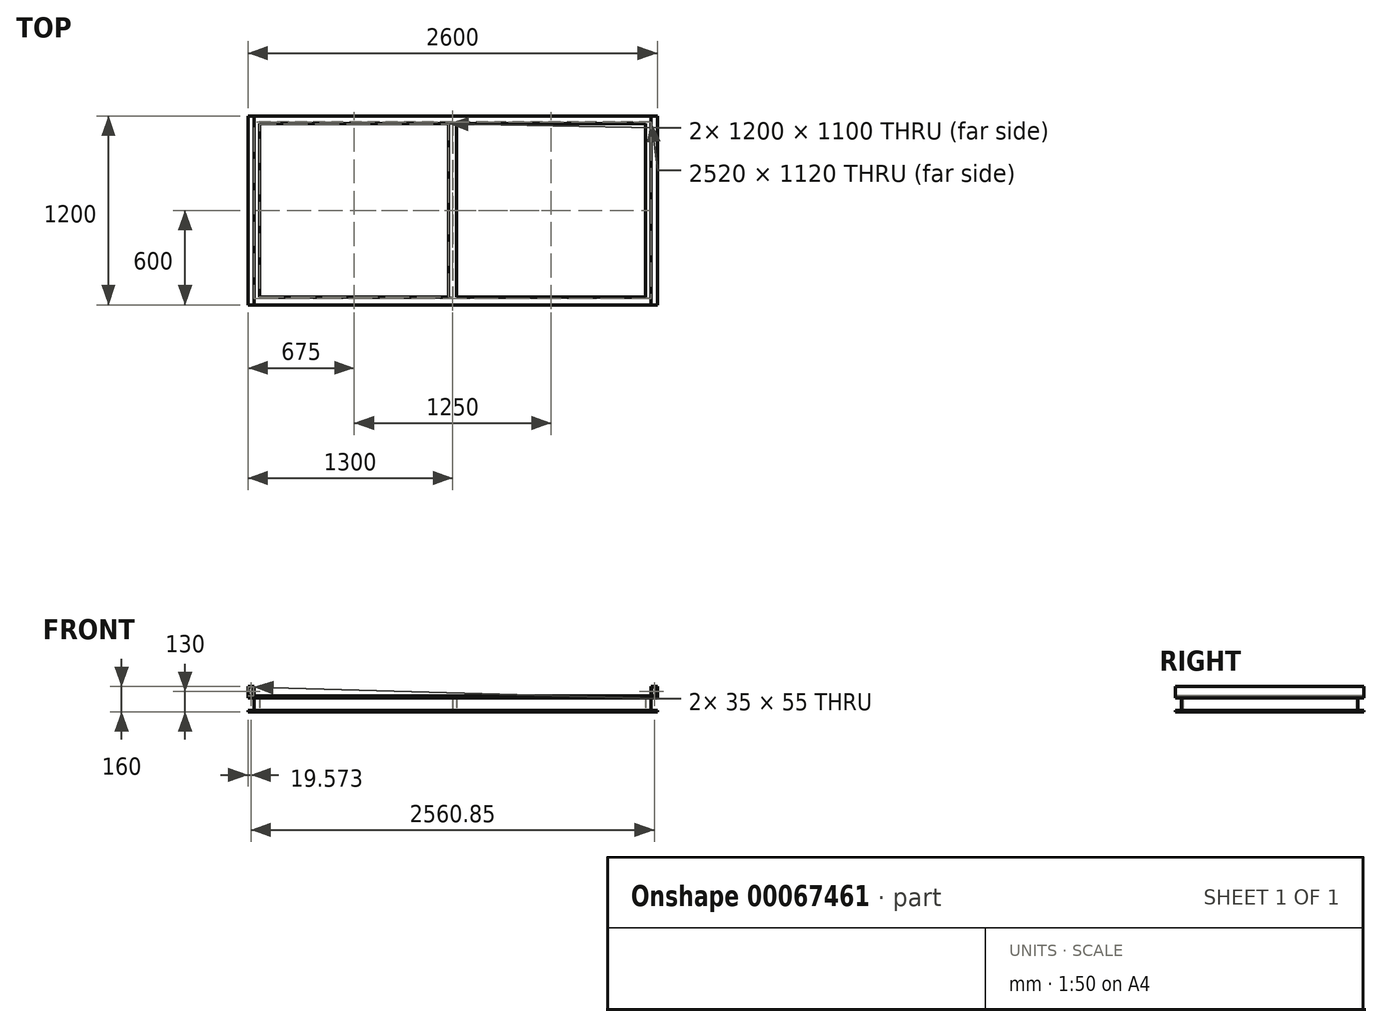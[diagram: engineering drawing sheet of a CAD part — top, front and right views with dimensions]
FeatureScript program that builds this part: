
annotation { "Feature Type Name" : "Feature", "Feature Type Description" : "" }
export const myFeature = defineFeature(function(context is Context, id is Id, definition is map)
    precondition{}
    {
        {
            var Q0;
            Q0=qCreatedBy(makeId("Top.planeOp"),FACE);
            var sketch = newSketch(context, id + "F0", { "sketchPlane" : qUnion([Q0])});
            skLineSegment(sketch, "E0.rect.bottom", {"start": v(1300, 600) * mm, "end": v(-1300, 600) * mm});
            skLineSegment(sketch, "E0.rect.top", {"start": v(1300, -600) * mm, "end": v(-1300, -600) * mm});
            skLineSegment(sketch, "E0.rect.left", {"start": v(1300, 600) * mm, "end": v(1300, -600) * mm});
            skLineSegment(sketch, "E0.rect.right", {"start": v(-1300, 600) * mm, "end": v(-1300, -600) * mm});
            skPoint(sketch, "E0.rect.middle", {"position": v(0, 0) * mm});
            skLineSegment(sketch, "E1.rect.bottom", {"start": v(1225, 550) * mm, "end": v(25, 550) * mm});
            skLineSegment(sketch, "E1.rect.top", {"start": v(1225, -550) * mm, "end": v(25, -550) * mm});
            skLineSegment(sketch, "E1.rect.left", {"start": v(1225, 550) * mm, "end": v(1225, -550) * mm});
            skLineSegment(sketch, "E1.rect.right", {"start": v(-1225, 550) * mm, "end": v(-1225, -550) * mm});
            skLineSegment(sketch, "E2.rect.left", {"start": v(25, 550) * mm, "end": v(25, -550) * mm});
            skLineSegment(sketch, "E2.rect.right", {"start": v(-25, 550) * mm, "end": v(-25, -550) * mm});
            skLineSegment(sketch, "E3.trimOffspring", {"start": v(-25, 550) * mm, "end": v(-1225, 550) * mm});
            skLineSegment(sketch, "E4.trimOffspring", {"start": v(-25, -550) * mm, "end": v(-1225, -550) * mm});
            skSolve(sketch);
        }
        {
            var Q0;
            Q0=makeQuery(id+"F0.imprint","IMPRINT",FACE,{"disambiguationData":[TD([[makeQuery(id+"F0.imprint","IMPRINT",EDGE,{"derivedFrom":sQuery(id+"F0.wireOp",EDGE,"E0.rect.bottom")}),1.0]])]});
            extrude(context, id + "F1", {"entities" : qUnion([Q0]), "depth" : 100 * mm});
        }
        {
            var Q0;
            Q0=makeQuery(id+"F1.opExtrude","SWEPT_FACE",FACE,{"disambiguationData":[OSD([sQuery(id+"F0.wireOp",EDGE,"E0.rect.right")])]});
            var sketch = newSketch(context, id + "F2", { "sketchPlane" : qUnion([Q0])});
            skLineSegment(sketch, "E5.bottom", {"start": v(-600, 90) * mm, "end": v(-560, 90) * mm});
            skLineSegment(sketch, "E5.top", {"start": v(-600, 10) * mm, "end": v(-560, 10) * mm});
            skLineSegment(sketch, "E5.left", {"start": v(-600, 90) * mm, "end": v(-600, 10) * mm});
            skLineSegment(sketch, "E5.right", {"start": v(-560, 90) * mm, "end": v(-560, 10) * mm});
            skLineSegment(sketch, "E6.bottom", {"start": v(600, 90) * mm, "end": v(560, 90) * mm});
            skLineSegment(sketch, "E6.top", {"start": v(600, 10) * mm, "end": v(560, 10) * mm});
            skLineSegment(sketch, "E6.left", {"start": v(600, 90) * mm, "end": v(600, 10) * mm});
            skLineSegment(sketch, "E6.right", {"start": v(560, 90) * mm, "end": v(560, 10) * mm});
            skSolve(sketch);
        }
        {
            var Q0;
            Q0=makeQuery(id+"F2.imprint","IMPRINT",FACE,{"disambiguationData":[TD([[makeQuery(id+"F2.imprint","IMPRINT",EDGE,{"derivedFrom":sQuery(id+"F2.wireOp",EDGE,"E5.bottom")}),-1.0]])]});
            var Q1;
            Q1=makeQuery(id+"F2.imprint","IMPRINT",FACE,{"disambiguationData":[TD([[makeQuery(id+"F2.imprint","IMPRINT",EDGE,{"derivedFrom":sQuery(id+"F2.wireOp",EDGE,"E6.bottom")}),1.0]])]});
            extrude(context, id + "F3", {"entities" : qUnion([Q0, Q1]), "operationType" : NewBodyOperationType.REMOVE, "endBound" : BoundingType.THROUGH_ALL, "oppositeDirection" : true, "depth" : 25 * mm});
        }
        {
            var Q0;
            Q0=makeQuery(id+"F3.boolean.opBoolean","COPY",FACE,{"derivedFrom":makeQuery(id+"F3.opExtrude","SWEPT_FACE",FACE,{"disambiguationData":[OSD([sQuery(id+"F2.wireOp",EDGE,"E6.right")])]})});
            var sketch = newSketch(context, id + "F4", { "sketchPlane" : qUnion([Q0])});
            skLineSegment(sketch, "E7.bottom", {"start": v(1300, 90) * mm, "end": v(1260, 90) * mm});
            skLineSegment(sketch, "E7.top", {"start": v(1300, 10) * mm, "end": v(1260, 10) * mm});
            skLineSegment(sketch, "E7.left", {"start": v(1300, 90) * mm, "end": v(1300, 10) * mm});
            skLineSegment(sketch, "E7.right", {"start": v(1260, 90) * mm, "end": v(1260, 10) * mm});
            skLineSegment(sketch, "E8.bottom", {"start": v(-1300, 90) * mm, "end": v(-1260, 90) * mm});
            skLineSegment(sketch, "E8.top", {"start": v(-1300, 10) * mm, "end": v(-1260, 10) * mm});
            skLineSegment(sketch, "E8.left", {"start": v(-1300, 90) * mm, "end": v(-1300, 10) * mm});
            skLineSegment(sketch, "E8.right", {"start": v(-1260, 90) * mm, "end": v(-1260, 10) * mm});
            skSolve(sketch);
        }
        {
            var Q0;
            Q0=makeQuery(id+"F4.imprint","IMPRINT",FACE,{"disambiguationData":[TD([[makeQuery(id+"F4.imprint","IMPRINT",EDGE,{"derivedFrom":sQuery(id+"F4.wireOp",EDGE,"E7.bottom")}),1.0]])]});
            var Q1;
            Q1=makeQuery(id+"F4.imprint","IMPRINT",FACE,{"disambiguationData":[TD([[makeQuery(id+"F4.imprint","IMPRINT",EDGE,{"derivedFrom":sQuery(id+"F4.wireOp",EDGE,"E8.bottom")}),1.0]])]});
            extrude(context, id + "F5", {"entities" : qUnion([Q0, Q1]), "operationType" : NewBodyOperationType.REMOVE, "endBound" : BoundingType.THROUGH_ALL, "oppositeDirection" : true, "depth" : 25 * mm});
        }
        {
            var Q0;
            Q0=qCreatedBy(makeId("Front.planeOp"),FACE);
            var sketch = newSketch(context, id + "F6", { "sketchPlane" : qUnion([Q0])});
            skLineSegment(sketch, "E9.bottom", {"start": v(0, 10) * mm, "end": v(-90, 10) * mm});
            skLineSegment(sketch, "E9.top", {"start": v(0, 90) * mm, "end": v(-90, 90) * mm});
            skLineSegment(sketch, "E9.left", {"start": v(0, 10) * mm, "end": v(0, 90) * mm});
            skLineSegment(sketch, "E9.right", {"start": v(-90, 10) * mm, "end": v(-90, 90) * mm});
            skSolve(sketch);
        }
        {
            var Q0;
            Q0 = qSketchRegion(id + "F6", true);
            var Q1;
            Q1=makeQuery(id+"F1.opExtrude","SWEPT_FACE",FACE,{"disambiguationData":[OSD([sQuery(id+"F0.wireOp",EDGE,"E3.trimOffspring")])]});
            var Q2;
            Q2=makeQuery(id+"F1.opExtrude","SWEPT_FACE",FACE,{"disambiguationData":[OSD([sQuery(id+"F0.wireOp",EDGE,"E4.trimOffspring")])]});
            extrude(context, id + "F7", {"entities" : qUnion([Q0]), "operationType" : NewBodyOperationType.REMOVE, "endBound" : BoundingType.UP_TO_SURFACE, "oppositeDirection" : true, "endBoundEntityFace" : qUnion([Q1]), "depth" : 25 * mm, "hasSecondDirection" : true, "secondDirectionBound" : SecondDirectionBoundingType.UP_TO_SURFACE, "secondDirectionOppositeDirection" : false, "secondDirectionBoundEntityFace" : qUnion([Q2]), "secondDirectionDepth" : 25 * mm});
        }
        {
            var Q0;
            Q0=makeQuery(id+"F1.opExtrude","CAP_FACE",FACE,{"disambiguationData":[OSD([sQuery(id+"F0.wireOp",EDGE,"E0.rect.bottom"),sQuery(id+"F0.wireOp",EDGE,"E0.rect.top"),sQuery(id+"F0.wireOp",EDGE,"E0.rect.left"),sQuery(id+"F0.wireOp",EDGE,"E0.rect.right"),sQuery(id+"F0.wireOp",EDGE,"E1.rect.bottom"),sQuery(id+"F0.wireOp",EDGE,"E1.rect.top"),sQuery(id+"F0.wireOp",EDGE,"E1.rect.left"),sQuery(id+"F0.wireOp",EDGE,"E1.rect.right"),sQuery(id+"F0.wireOp",EDGE,"E2.rect.left"),sQuery(id+"F0.wireOp",EDGE,"E2.rect.right"),sQuery(id+"F0.wireOp",EDGE,"E3.trimOffspring"),sQuery(id+"F0.wireOp",EDGE,"E4.trimOffspring")])],"isStart":false});
            var sketch = newSketch(context, id + "F8", { "sketchPlane" : qUnion([Q0])});
            skLineSegment(sketch, "E10.bottom", {"start": v(1300, 600) * mm, "end": v(1260, 600) * mm});
            skLineSegment(sketch, "E10.top", {"start": v(1300, -600) * mm, "end": v(1260, -600) * mm});
            skLineSegment(sketch, "E10.left", {"start": v(1300, 600) * mm, "end": v(1300, -600) * mm});
            skLineSegment(sketch, "E10.right", {"start": v(1260, 600) * mm, "end": v(1260, -600) * mm});
            skLineSegment(sketch, "E11.bottom", {"start": v(-1300, 600) * mm, "end": v(-1260, 600) * mm});
            skLineSegment(sketch, "E11.top", {"start": v(-1300, -600) * mm, "end": v(-1260, -600) * mm});
            skLineSegment(sketch, "E11.left", {"start": v(-1300, 600) * mm, "end": v(-1300, -600) * mm});
            skLineSegment(sketch, "E11.right", {"start": v(-1260, 600) * mm, "end": v(-1260, -600) * mm});
            skSolve(sketch);
        }
        {
            var Q0;
            Q0=makeQuery(id+"F8.imprint","IMPRINT",FACE,{"disambiguationData":[TD([[makeQuery(id+"F8.imprint","IMPRINT",EDGE,{"derivedFrom":sQuery(id+"F8.wireOp",EDGE,"E11.bottom")}),1.0]])]});
            var Q1;
            Q1=makeQuery(id+"F8.imprint","IMPRINT",FACE,{"disambiguationData":[TD([[makeQuery(id+"F8.imprint","IMPRINT",EDGE,{"derivedFrom":sQuery(id+"F8.wireOp",EDGE,"E10.bottom")}),1.0]])]});
            extrude(context, id + "F9", {"entities" : qUnion([Q0, Q1]), "operationType" : NewBodyOperationType.ADD, "depth" : 60 * mm});
        }
        {
            var Q0;
            {var subQ2=sQuery(id+"F0.wireOp",EDGE,"E0.rect.top");Q0=makeQuery(id+"F9.boolean.opBoolean","MERGE",FACE,{"derivedFrom":[makeQuery(id+"F3.boolean.opBoolean","SPLIT",FACE,{"disambiguationData":[TD([makeQuery(id+"F3.opExtrude","SWEPT_FACE",FACE,{"disambiguationData":[OSD([sQuery(id+"F2.wireOp",EDGE,"E6.bottom")])]})])],"derivedFrom":makeQuery(id+"F1.opExtrude","SWEPT_FACE",FACE,{"disambiguationData":[OSD([subQ2])]})}),makeQuery(id+"F9.opExtrude","SWEPT_FACE",FACE,{"disambiguationData":[OSD([sQuery(id+"F8.wireOp",EDGE,"E10.top")])]}),makeQuery(id+"F9.opExtrude","SWEPT_FACE",FACE,{"disambiguationData":[OSD([sQuery(id+"F8.wireOp",EDGE,"E11.top")])]})]});}
            var sketch = newSketch(context, id + "F10", { "sketchPlane" : qUnion([Q0])});
            skLineSegment(sketch, "E12.bottom", {"start": v(-1297.93, 157.5) * mm, "end": v(-1262.93, 157.5) * mm});
            skLineSegment(sketch, "E12.top", {"start": v(-1297.93, 102.5) * mm, "end": v(-1262.93, 102.5) * mm});
            skLineSegment(sketch, "E12.left", {"start": v(-1297.93, 157.5) * mm, "end": v(-1297.93, 102.5) * mm});
            skLineSegment(sketch, "E12.right", {"start": v(-1262.93, 157.5) * mm, "end": v(-1262.93, 102.5) * mm});
            skLineSegment(sketch, "E13.MirrorCS", {"start": v(1297.93, 157.5) * mm, "end": v(1297.93, 102.5) * mm});
            skLineSegment(sketch, "E14.MirrorCS", {"start": v(1297.93, 102.5) * mm, "end": v(1262.93, 102.5) * mm});
            skLineSegment(sketch, "E15.MirrorCS", {"start": v(1297.93, 157.5) * mm, "end": v(1262.93, 157.5) * mm});
            skLineSegment(sketch, "E16.MirrorCS", {"start": v(1262.93, 157.5) * mm, "end": v(1262.93, 102.5) * mm});
            skSolve(sketch);
        }
        {
            var Q0;
            Q0=makeQuery(id+"F10.imprint","IMPRINT",FACE,{"disambiguationData":[TD([[makeQuery(id+"F10.imprint","IMPRINT",EDGE,{"derivedFrom":sQuery(id+"F10.wireOp",EDGE,"E13.MirrorCS")}),-1.0]])]});
            var Q1;
            Q1=makeQuery(id+"F10.imprint","IMPRINT",FACE,{"disambiguationData":[TD([[makeQuery(id+"F10.imprint","IMPRINT",EDGE,{"derivedFrom":sQuery(id+"F10.wireOp",EDGE,"E12.bottom")}),-1.0]])]});
            extrude(context, id + "F11", {"entities" : qUnion([Q0, Q1]), "operationType" : NewBodyOperationType.REMOVE, "endBound" : BoundingType.THROUGH_ALL, "oppositeDirection" : true, "depth" : 25 * mm});
        }
    });
